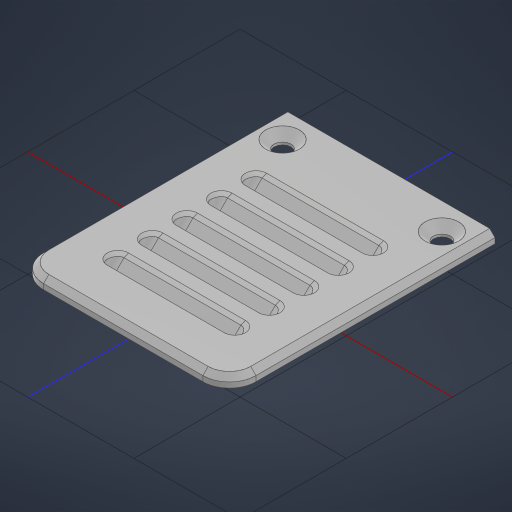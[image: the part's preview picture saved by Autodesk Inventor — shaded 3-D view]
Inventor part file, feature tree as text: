
AUTODESK INVENTOR PART (.ipt)
format: ipt  version: 2023.2 (Build 272271030, 271C)  size: 380,928 bytes
history: native  units: mm
features: sketch x2, extrude x2, chamfer x2, loft x1, pattern_linear x1, hole x1, projected_geometry x1
ambient origin geometry x8: Origin, YZ Plane, XZ Plane, XY Plane, X Axis, Y Axis, Z Axis, Center Point
bodies: Volumenkörper1 (feature_tree)
feature tree (10):
  sketch  "Skizze1"  dims[d3=40.0mm d7=5.0mm]
  extrude  "Extrusion1"  Depth=5.0mm
  extrude  "Extrusion7"  Depth=2.0mm
  sketch  "Skizze5"  dims[d15=2.0mm d16=0.0mm d18=2.0mm d34=1.0mm d35=2.0mm d36=45.0deg d41=12.0mm d42=2.0mm d43=2.0mm d44=26.0mm d49=22.0mm d50=3.0mm d51=25.0mm d60=10.0mm d62=2.0mm d64=2.0mm d65=26.0mm d66=0.1mm d67=1.0mm d68=1.0mm d69=0.0mm d70=3.0mm d71=25.0mm d72=10.0mm d80=8.0mm d81=0.0mm d82=90.0deg d83=0.0mm d84=90.0deg d102=0.5mm d103=2.0mm d104=45.0deg d105=50.0mm d107=6.5mm d115=10.0mm d116=3.2mm d117=6.0mm d118=6.3mm d119=2.0mm d120=90.0deg d121=7.0mm d122=0.0mm d123=10.0mm d124=4.5mm]
  loft  "Erhebung1"
  pattern_linear  "Rechteckige Anordnung1"  Spacing1=12.0mm  [1 undecoded]
  hole  "Bohrung3"  [1 undecoded]
  chamfer  "Fase1"  Distance=2.0mm
  chamfer  "Fase2"  Distance=26.0mm
  projected_geometry  "Projizierte Kontur4"
note: 2 required parameter values undecoded (feature->parameter linkage not recoverable at this tier; creation-order binding heuristic only, values carry confidence <= 0.55)
